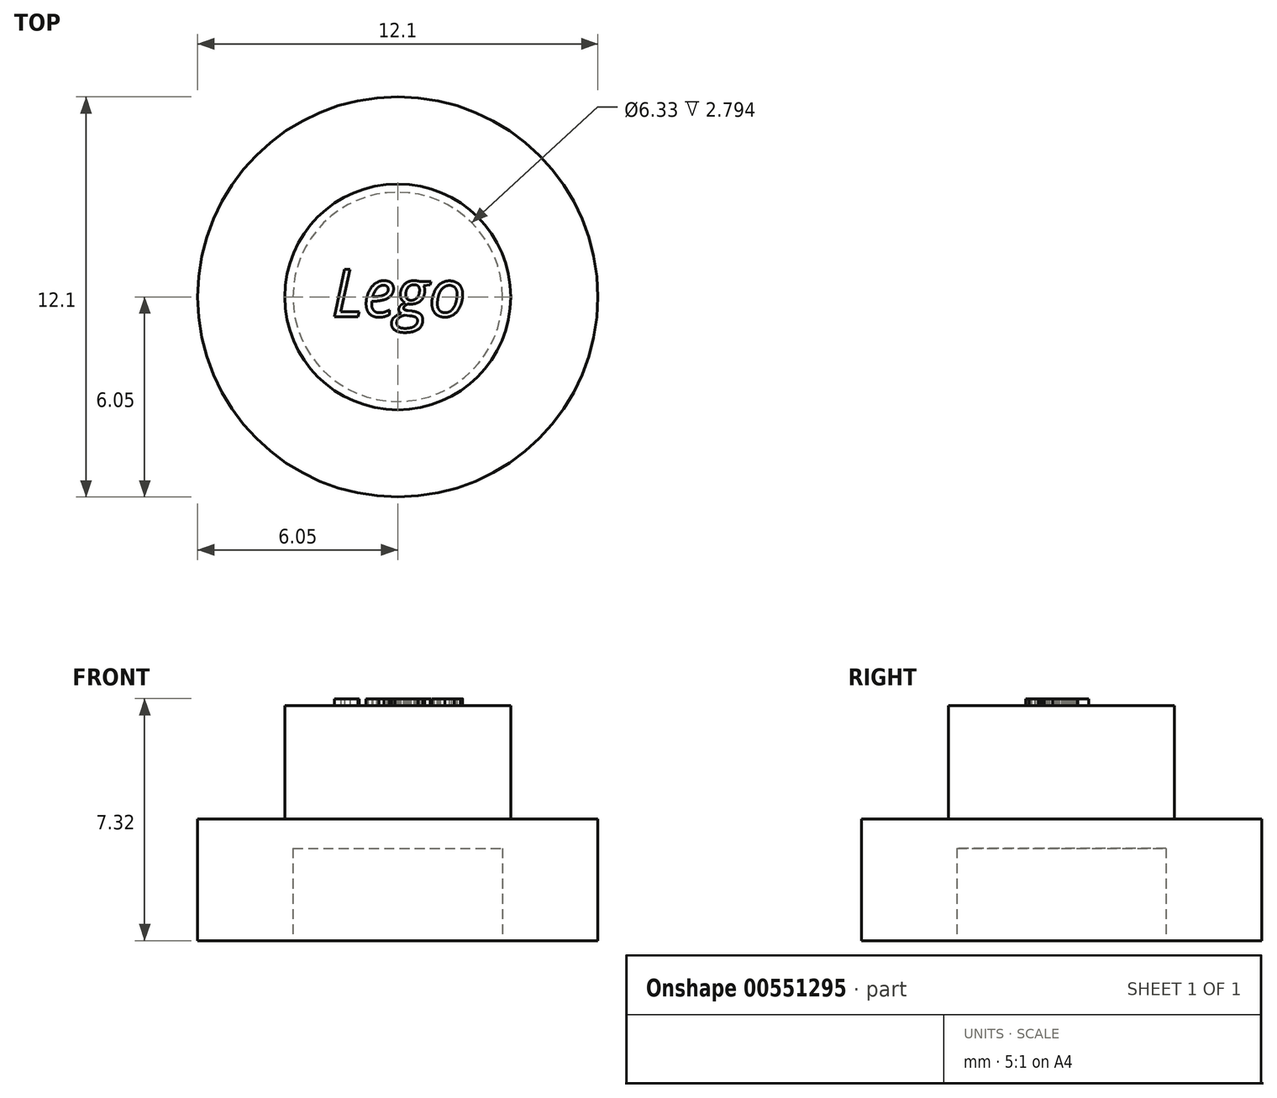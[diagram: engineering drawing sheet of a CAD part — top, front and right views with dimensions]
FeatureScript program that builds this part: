
annotation { "Feature Type Name" : "Feature", "Feature Type Description" : "" }
export const myFeature = defineFeature(function(context is Context, id is Id, definition is map)
    precondition{}
    {
        {
            var Q0;
            Q0=qCreatedBy(makeId("Top.planeOp"),FACE);
            var sketch = newSketch(context, id + "F0", { "sketchPlane" : qUnion([Q0])});
            skCircle(sketch, "E0", {"center": v(0, 0) * mm, "radius": 6.05 * mm});
            skSolve(sketch);
        }
        {
            var Q0;
            Q0=makeQuery(id+"F0.imprint","IMPRINT",FACE,{"disambiguationData":[TD([[makeQuery(id+"F0.imprint","IMPRINT",EDGE,{"derivedFrom":sQuery(id+"F0.wireOp",EDGE,"E0")}),1.0]])]});
            extrude(context, id + "F1", {"entities" : qUnion([Q0]), "depth" : 3.68 * mm, "offsetDistance" : 25.4 * mm});
        }
        {
            var Q0;
            Q0=makeQuery(id+"F1.opExtrude","CAP_FACE",FACE,{"disambiguationData":[OSD([sQuery(id+"F0.wireOp",EDGE,"E0")])],"isStart":false});
            var sketch = newSketch(context, id + "F2", { "sketchPlane" : qUnion([Q0])});
            skCircle(sketch, "E1", {"center": v(0, 0) * mm, "radius": 3.42 * mm});
            skSolve(sketch);
        }
        {
            var Q0;
            Q0=makeQuery(id+"F2.imprint","IMPRINT",FACE,{"disambiguationData":[TD([[makeQuery(id+"F2.imprint","IMPRINT",EDGE,{"derivedFrom":sQuery(id+"F2.wireOp",EDGE,"E1")}),1.0]])]});
            extrude(context, id + "F3", {"entities" : qUnion([Q0]), "operationType" : NewBodyOperationType.ADD, "depth" : 3.43 * mm, "offsetDistance" : 25.4 * mm});
        }
        {
            var Q0;
            Q0=makeQuery(id+"F1.opExtrude","CAP_FACE",FACE,{"disambiguationData":[OSD([sQuery(id+"F0.wireOp",EDGE,"E0")])],"isStart":true});
            var sketch = newSketch(context, id + "F4", { "sketchPlane" : qUnion([Q0])});
            skCircle(sketch, "E2", {"center": v(0, 0) * mm, "radius": 3.17 * mm});
            skSolve(sketch);
        }
        {
            var Q0;
            Q0=makeQuery(id+"F4.imprint","IMPRINT",FACE,{"disambiguationData":[TD([[makeQuery(id+"F4.imprint","IMPRINT",EDGE,{"derivedFrom":sQuery(id+"F4.wireOp",EDGE,"E2")}),1.0]])]});
            extrude(context, id + "F5", {"entities" : qUnion([Q0]), "operationType" : NewBodyOperationType.REMOVE, "oppositeDirection" : true, "depth" : 2.8 * mm, "offsetDistance" : 25.4 * mm});
        }
        {
            var Q0;
            Q0=makeQuery(id+"F3.opExtrude","CAP_FACE",FACE,{"disambiguationData":[OSD([sQuery(id+"F2.wireOp",EDGE,"E1")])],"isStart":false});
            var sketch = newSketch(context, id + "F6", { "sketchPlane" : qUnion([Q0])});
            skText(sketch, "E3", { "text": "Lego", "fontName": "OpenSans-Italic.ttf"});
            const initialGuessF6  = {"E3": [-0.002, -0.0006, 1, 0, 0.00144]};
            skSetInitialGuess(sketch, initialGuessF6);
            skSolve(sketch);
        }
        {
            var Q0;
            Q0 = qSketchRegion(id + "F6", true);
            extrude(context, id + "F7", {"entities" : qUnion([Q0]), "operationType" : NewBodyOperationType.ADD, "depth" : 0.2 * mm, "offsetDistance" : 25.4 * mm});
        }
    });
